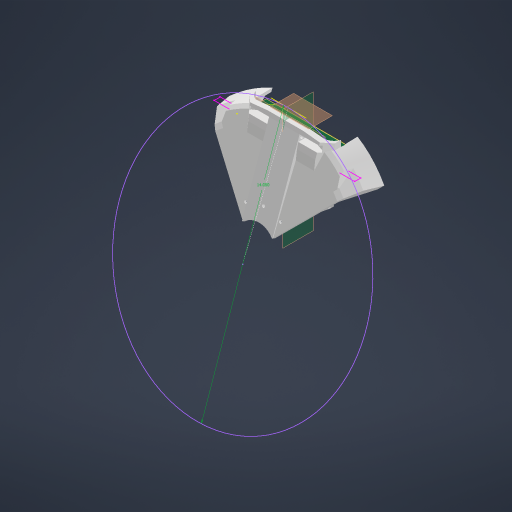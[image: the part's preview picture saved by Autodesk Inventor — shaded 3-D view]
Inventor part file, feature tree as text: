
AUTODESK INVENTOR PART (.ipt)
format: ipt  version: 2024 (Build 280153000, 153)  size: 772,096 bytes
history: native  units: in
note: dims shown in document units (in); Inventor stores cm internally (conversion verified against a paired STEP export)
features: reference x30, projected_geometry x25, sketch x23, extrude x20, plane x8, other x5, revolve x3, chamfer x3, mirror x2, fillet x1
ambient origin geometry x8: Origin, YZ Plane, XZ Plane, XY Plane, X Axis, Y Axis, Z Axis, Center Point
bodies: Solid1 (feature_tree)
feature tree (120):
  plane  "Work Plane1"
  other  "Work Point1"
  extrude  "Extrusion1"  Depth=12.0in
  plane  "Work Plane6"
  extrude  "Extrusion2"  Depth=1.2205in
  extrude  "Extrusion3"  Depth=1.0in TaperAngle=0.0deg
  plane  "Work Plane2"
  sketch  "Sketch8"  dims[d10=0.2559in d11=0.1378in d12=0.0in]
  plane  "Work Plane3"
  plane  "Work Plane4"
  plane  "Work Plane5"
  plane  "Work Plane7"
  extrude  "Extrusion14"  Depth=0.1378in TaperAngle=0.0deg
  extrude  "Extrusion15"  Depth=0.1654in
  sketch  "Sketch21"  dims[d78=1.0in d79=0.0in d80=1.0in d81=0.0in]
  revolve  "Revolution1"  Angle=90.0deg
  plane  "Work Plane8"
  extrude  "Extrusion16"  Depth=1.0in TaperAngle=0.0deg
  sketch  "Sketch24"  dims[d86=0.0197in d87=1.0in d88=0.0in]
  extrude  "Extrusion17"  Depth=0.1673in
  extrude  "Extrusion18"  TaperAngle=360.0deg  [1 undecoded]
  sketch  "Sketch26"  dims[d93=14.0in d94=0.2955in]
  extrude  "Extrusion19"  Depth=1.0in TaperAngle=0.0deg
  extrude  "Extrusion20"  Depth=3.5in TaperAngle=0.0deg
  extrude  "Extrusion21"  Depth=0.2955in
  revolve  "Revolution2"  [1 undecoded]
  extrude  "Extrusion22"  Depth=0.845in TaperAngle=0.0deg
  chamfer  "Chamfer8"  Distance=0.845in
  sketch  "Sketch32"  dims[d103=0.1168in]
  revolve  "Revolution4"  [1 undecoded]
  chamfer  "Chamfer9"  Distance=0.5in
  fillet  "Fillet3"  Radius=0.25in
  mirror  "Mirror2"
  chamfer  "Chamfer10"  Distance=0.1575in
  extrude  "Extrusion23"  Depth=0.2362in TaperAngle=0.0deg
  extrude  "Extrusion24"  Depth=0.2362in TaperAngle=0.0deg
  extrude  "Extrusion25"  Depth=0.1181in TaperAngle=0.0deg
  extrude  "Extrusion27"  Depth=0.1181in TaperAngle=0.0deg
  extrude  "Extrusion28"  Depth=0.2362in
  extrude  "Extrusion29"  Depth=0.2362in TaperAngle=0.0deg
  extrude  "Extrusion30"  Depth=0.2362in TaperAngle=360.0deg
  extrude  "Extrusion31"  Depth=0.2362in TaperAngle=0.0deg
  mirror  "Mirror3"
  sketch  "Sketch2"  dims[d0=0.0157in d1=12.0in]
  reference  "Reference1"
  reference  "Reference2"
  reference  "Reference3"
  reference  "Reference4"
  reference  "Reference5"
  reference  "Reference6"
  reference  "Reference7"
  sketch  "Sketch3"  dims[d3=0.4626in d5=1.2205in]
  reference  "Reference8"
  sketch  "Sketch6"  dims[d6=1.0in d7=0.0in d8=1.0in d9=0.0in]
  projected_geometry  "Projected Loop1"
  reference  "Reference9"
  reference  "Reference10"
  reference  "Reference11"
  reference  "Reference12"
  reference  "Reference13"
  reference  "Reference20"
  reference  "Reference21"
  reference  "Reference22"
  sketch  "Sketch19"  dims[d35=60.0deg d50=0.1654in]
  projected_geometry  "Projected Loop16"
  reference  "Reference23"
  reference  "Reference24"
  reference  "Reference25"
  sketch  "Sketch20"  dims[d76=0.1512in d77=90.0deg]
  projected_geometry  "Projected Loop17"
  projected_geometry  "Projected Loop18"
  projected_geometry  "Projected Loop19"
  reference  "Reference26"
  sketch  "Sketch22"  dims[d82=14.0in d83=0.1673in]
  reference  "Reference27"
  reference  "Reference28"
  reference  "Reference29"
  sketch  "Sketch23"  dims[d84=6.533in d85=360.0deg]
  reference  "Reference30"
  reference  "Reference31"
  reference  "Reference32"
  projected_geometry  "Projected Loop20"
  reference  "Reference33"
  reference  "Reference34"
  projected_geometry  "Projected Loop21"
  reference  "Reference35"
  reference  "Reference36"
  sketch  "Sketch25"  dims[d89=1.0in d90=0.0in d91=3.5in d92=0.0in]
  projected_geometry  "Projected Loop22"
  projected_geometry  "Projected Loop23"
  projected_geometry  "Projected Loop24"
  projected_geometry  "Projected Loop25"
  projected_geometry  "Projected Loop26"
  projected_geometry  "Projected Loop27"
  sketch  "Sketch27"  dims[d95=3.5in d96=0.0in d97=0.1575in d98=0.0in]
  projected_geometry  "Projected Loop28"
  sketch  "Sketch28"  dims[d99=0.1654in d100=0.845in d101=0.0in]
  projected_geometry  "Projected Loop29"
  sketch  "Sketch30"  dims[d102=0.3937in]
  projected_geometry  "Projected Loop31"
  projected_geometry  "Projected Loop32"
  sketch  "Sketch33"  dims[d104=0.7in d107=0.845in d108=0.0in]
  projected_geometry  "Projected Loop33"
  sketch  "Sketch35"  dims[d109=0.5162in d110=0.125in d111=0.0687in d113=0.1654in]
  projected_geometry  "Projected Loop34"
  sketch  "Sketch36"  dims[d114=2.0in]
  projected_geometry  "Projected Loop35"
  projected_geometry  "Projected Loop36"
  sketch  "Sketch38"  dims[d119=0.6in]
  projected_geometry  "Projected Loop38"
  sketch  "Sketch39"  dims[d120=0.6in]
  projected_geometry  "Projected Loop39"
  projected_geometry  "Projected Loop40"
  sketch  "Sketch40"  dims[d121=0.0344in d122=0.5in d123=0.125in d124=0.0687in d125=0.25in d126=0.1575in d127=0.125in d128=0.0687in]
  sketch  "Sketch41"  dims[d129=1.0in d130=0.0in d131=11.4375in d132=0.0in d133=0.75in d134=0.0in d137=0.1181in d138=0.0in d139=0.1181in d140=0.0in d141=2.5in d142=0.9306in d143=0.0in d144=4.7244in d146=360.0deg d148=0.9306in d149=0.0in d150=0.2441in d151=0.252in d152=0.1654in d153=0.2362in d154=0.0in]
  projected_geometry  "Projected Loop41"
  other  "<userpath>\Desktop\SeniorDesign\Head_Assembly.iam"
  other  "Head_Assembly.iam"
  other  "Emeet_Camera:1"
  other  "Assembly1"
note: 3 required parameter values undecoded (feature->parameter linkage not recoverable at this tier; creation-order binding heuristic only, values carry confidence <= 0.55)